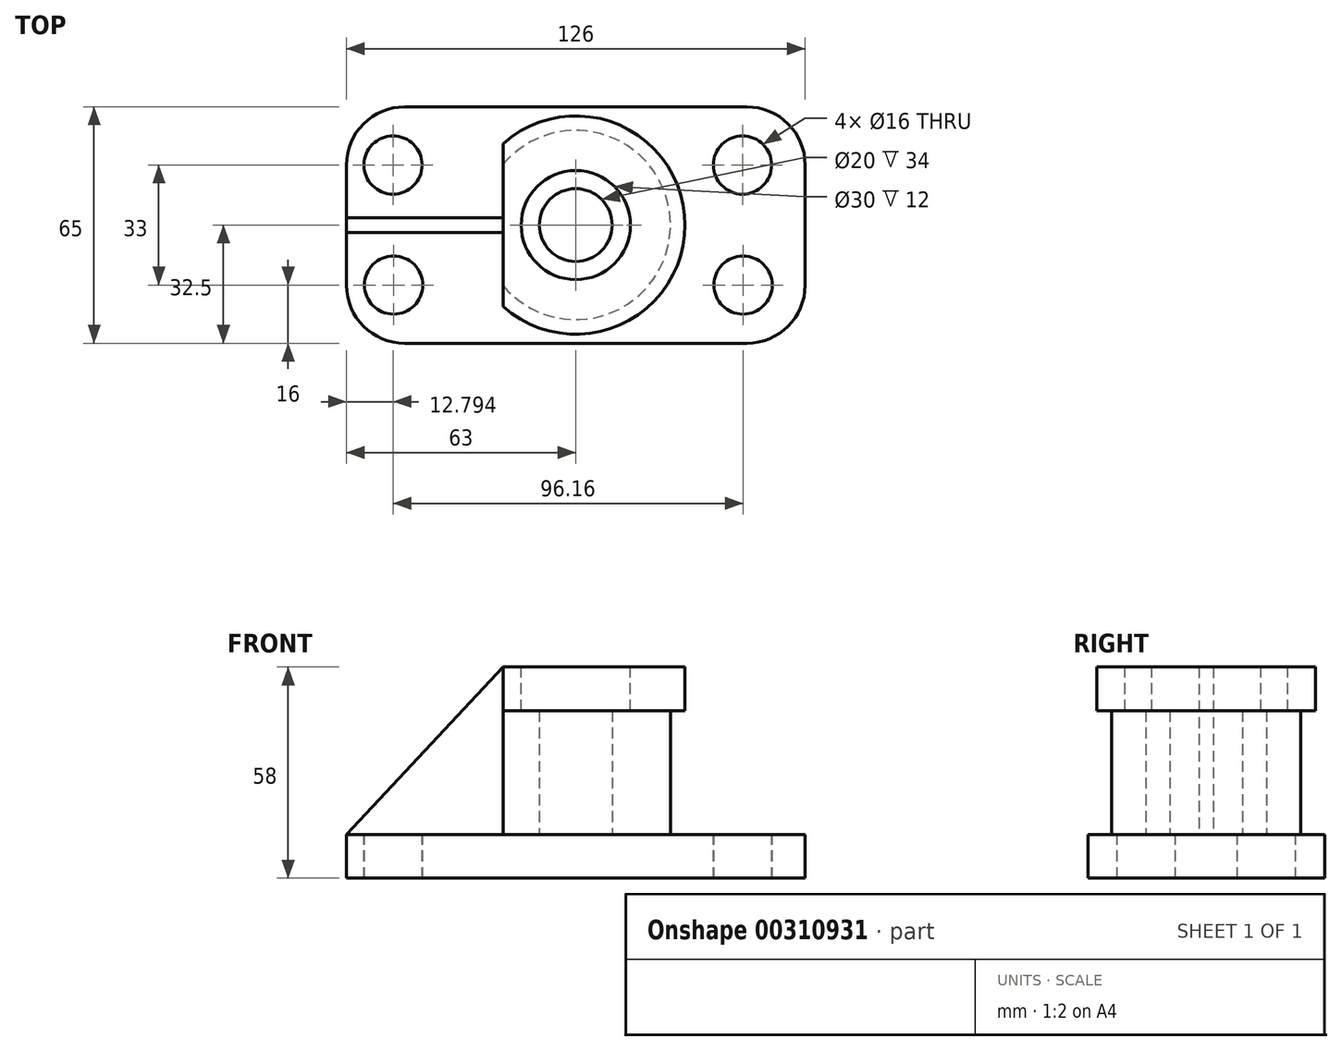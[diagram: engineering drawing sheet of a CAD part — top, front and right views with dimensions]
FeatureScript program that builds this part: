
annotation { "Feature Type Name" : "Feature", "Feature Type Description" : "" }
export const myFeature = defineFeature(function(context is Context, id is Id, definition is map)
    precondition{}
    {
        {
            var Q0;
            Q0=qCreatedBy(makeId("Top.planeOp"),FACE);
            var sketch = newSketch(context, id + "F0", { "sketchPlane" : qUnion([Q0])});
            skCircle(sketch, "E0", {"center": v(0, 0) * mm, "radius": 26 * mm});
            skCircle(sketch, "E1", {"center": v(0, 0) * mm, "radius": 10 * mm});
            skPoint(sketch, "E2", {"position": v(-10, 0) * mm});
            skLineSegment(sketch, "E3", {"start": v(-10, 24) * mm, "end": v(-10, -24) * mm});
            skSolve(sketch);
        }
        {
            var Q0;
            Q0 = qSketchRegion(id + "F0", true);
            extrude(context, id + "F1", {"entities" : qUnion([Q0]), "depth" : 58 * mm});
        }
        {
            var Q0;
            Q0=makeQuery(id+"F1.opExtrude","CAP_FACE",FACE,{"disambiguationData":[OSD([sQuery(id+"F0.wireOp",EDGE,"E0"),sQuery(id+"F0.wireOp",EDGE,"E1")])],"isStart":true});
            var sketch = newSketch(context, id + "F2", { "sketchPlane" : qUnion([Q0])});
            skLineSegment(sketch, "E4", {"start": v(0, 32.5) * mm, "end": v(-63, 32.5) * mm});
            skLineSegment(sketch, "E5", {"start": v(-63, 32.5) * mm, "end": v(-63, -32.5) * mm});
            skLineSegment(sketch, "E6", {"start": v(-63, -32.5) * mm, "end": v(63, -32.5) * mm});
            skLineSegment(sketch, "E7", {"start": v(63, 32.5) * mm, "end": v(63, -32.5) * mm});
            skLineSegment(sketch, "E8", {"start": v(63, 32.5) * mm, "end": v(0, 32.5) * mm});
            skPoint(sketch, "E9.end.orphan", {"position": v(-63, 0) * mm});
            skPoint(sketch, "E10.end.orphan", {"position": v(0, 0) * mm});
            skSolve(sketch);
        }
        {
            var Q0;
            Q0 = qSketchRegion(id + "F2", true);
            extrude(context, id + "F3", {"entities" : qUnion([Q0]), "operationType" : NewBodyOperationType.ADD, "oppositeDirection" : true, "depth" : 12 * mm});
        }
        {
            var Q0;
            {var subQ0=sQuery(id+"F2.wireOp",EDGE,"E6");var subQ1=sQuery(id+"F2.wireOp",EDGE,"E5");var subQ2=sQuery(id+"F2.wireOp",EDGE,"E8");var subQ3=sQuery(id+"F2.wireOp",EDGE,"E4");var subQ4=sQuery(id+"F2.wireOp",EDGE,"E7");Q0=makeQuery(id+"F3.boolean.opBoolean","SPLIT",FACE,{"disambiguationData":[TD([makeQuery(id+"F1.opExtrude","SWEPT_FACE",FACE,{"disambiguationData":[OSD([sQuery(id+"F0.wireOp",EDGE,"E0")])]})])],"derivedFrom":makeQuery(id+"F3.opExtrude","CAP_FACE",FACE,{"disambiguationData":[OSD([subQ3,subQ1,subQ0,subQ4,subQ2])],"isStart":false})});}
            var sketch = newSketch(context, id + "F4", { "sketchPlane" : qUnion([Q0])});
            skCircle(sketch, "E11", {"center": v(-50.05, -16.5) * mm, "radius": 8 * mm});
            skCircle(sketch, "E12", {"center": v(-50.2, 16.5) * mm, "radius": 8 * mm});
            skCircle(sketch, "E13", {"center": v(45.8, 16.5) * mm, "radius": 8 * mm});
            skCircle(sketch, "E14", {"center": v(45.95, -16.5) * mm, "radius": 8 * mm});
            skPoint(sketch, "E15.end.orphan", {"position": v(-63, 0) * mm});
            skPoint(sketch, "E15.start.orphan", {"position": v(0, 0) * mm});
            skSolve(sketch);
        }
        {
            var Q0;
            Q0 = qSketchRegion(id + "F4", true);
            extrude(context, id + "F5", {"entities" : qUnion([Q0]), "operationType" : NewBodyOperationType.REMOVE, "oppositeDirection" : true, "depth" : 25 * mm});
        }
        {
            var Q0;
            Q0=makeQuery(id+"F3.opExtrude","SWEPT_EDGE",EDGE,{"disambiguationData":[OSD([sQuery(id+"F2.wireOp",EDGE,"E5"),sQuery(id+"F2.wireOp",EDGE,"E6")])]});
            var Q1;
            Q1=makeQuery(id+"F3.opExtrude","SWEPT_EDGE",EDGE,{"disambiguationData":[OSD([sQuery(id+"F2.wireOp",EDGE,"E4"),sQuery(id+"F2.wireOp",EDGE,"E5")])]});
            var Q2;
            Q2=makeQuery(id+"F3.opExtrude","SWEPT_EDGE",EDGE,{"disambiguationData":[OSD([sQuery(id+"F2.wireOp",EDGE,"E6"),sQuery(id+"F2.wireOp",EDGE,"E7")])]});
            var Q3;
            Q3=makeQuery(id+"F3.opExtrude","SWEPT_EDGE",EDGE,{"disambiguationData":[OSD([sQuery(id+"F2.wireOp",EDGE,"E7"),sQuery(id+"F2.wireOp",EDGE,"E8")])]});
            fillet(context, id + "F6", {"entities" : qUnion([Q0, Q1, Q2, Q3]), "radius" : 16 * mm, "tangentPropagation" : true, "allowEdgeOverflow" : false});
        }
        {
            var Q0;
            Q0=makeQuery(id+"F1.opExtrude","CAP_FACE",FACE,{"disambiguationData":[OSD([sQuery(id+"F0.wireOp",EDGE,"E0"),sQuery(id+"F0.wireOp",EDGE,"E1")])],"isStart":false});
            var sketch = newSketch(context, id + "F7", { "sketchPlane" : qUnion([Q0])});
            skCircle(sketch, "E16", {"center": v(0, 0) * mm, "radius": 30 * mm});
            skPoint(sketch, "E17", {"position": v(-26, 0) * mm});
            skLineSegment(sketch, "E18", {"start": v(-20, 22.36) * mm, "end": v(-20, -22.36) * mm});
            skSolve(sketch);
        }
        {
            var Q0;
            Q0=makeQuery(id+"F7.imprint","IMPRINT",FACE,{"disambiguationData":[TD([[makeQuery(id+"F7.imprint","IMPRINT",EDGE,{"derivedFrom":makeQuery(id+"F1.opExtrude","CAP_EDGE",EDGE,{"disambiguationData":[OSD([sQuery(id+"F0.wireOp",EDGE,"E1")])],"isStart":false})}),1.0]])]});
            var Q1;
            {var subQ4=makeQuery(id+"F1.opExtrude","CAP_EDGE",EDGE,{"disambiguationData":[OSD([sQuery(id+"F0.wireOp",EDGE,"E0")])],"isStart":false});Q1=makeQuery(id+"F7.imprint","IMPRINT",FACE,{"disambiguationData":[TD([[makeQuery(id+"F7.imprint","IMPRINT",EDGE,{"derivedFrom":subQ4}),-1.0]])]});}
            var Q2;
            Q2=makeQuery(id+"F7.imprint","IMPRINT",FACE,{"disambiguationData":[TD([[makeQuery(id+"F7.imprint","IMPRINT",EDGE,{"derivedFrom":makeQuery(id+"F1.opExtrude","CAP_EDGE",EDGE,{"disambiguationData":[OSD([sQuery(id+"F0.wireOp",EDGE,"E0")])],"isStart":false})}),1.0]])]});
            extrude(context, id + "F8", {"entities" : qUnion([Q0, Q1, Q2]), "operationType" : NewBodyOperationType.ADD, "oppositeDirection" : true, "depth" : 12 * mm});
        }
        {
            var Q0;
            Q0=makeQuery(id+"F7.imprint","IMPRINT",FACE,{"disambiguationData":[TD([[makeQuery(id+"F7.imprint","IMPRINT",EDGE,{"derivedFrom":makeQuery(id+"F1.opExtrude","CAP_EDGE",EDGE,{"disambiguationData":[OSD([sQuery(id+"F0.wireOp",EDGE,"E0")])],"isStart":false})}),1.0]])]});
            var sketch = newSketch(context, id + "F9", { "sketchPlane" : qUnion([Q0])});
            skCircle(sketch, "E19", {"center": v(0, 0) * mm, "radius": 15 * mm});
            skSolve(sketch);
        }
        {
            var Q0;
            Q0=makeQuery(id+"F9.imprint","IMPRINT",FACE,{"disambiguationData":[TD([[makeQuery(id+"F9.imprint","IMPRINT",EDGE,{"derivedFrom":makeQuery(id+"F7.imprint","IMPRINT",EDGE,{"derivedFrom":makeQuery(id+"F1.opExtrude","CAP_EDGE",EDGE,{"disambiguationData":[OSD([sQuery(id+"F0.wireOp",EDGE,"E1")])],"isStart":false})})}),1.0]])]});
            var Q1;
            Q1=makeQuery(id+"F9.imprint","IMPRINT",FACE,{"disambiguationData":[TD([[makeQuery(id+"F9.imprint","IMPRINT",EDGE,{"derivedFrom":sQuery(id+"F9.wireOp",EDGE,"E19")}),1.0]])]});
            extrude(context, id + "F10", {"entities" : qUnion([Q0, Q1]), "operationType" : NewBodyOperationType.REMOVE, "oppositeDirection" : true, "depth" : 12 * mm});
        }
        {
            var Q0;
            {var subQ0=sQuery(id+"F7.wireOp",EDGE,"E18");var subQ1=sQuery(id+"F7.wireOp",EDGE,"E16");var subQ2=makeQuery(id+"F7.imprint","INTERSECT",VERTEX,{"disambiguationData":[OD(0.0)],"derivedFrom":[subQ1,subQ0]});Q0=makeQuery(id+"F7.imprint","IMPRINT",FACE,{"disambiguationData":[TD([[makeQuery(id+"F7.imprint","IMPRINT",EDGE,{"disambiguationData":[TD([[subQ2,-1.0]])],"derivedFrom":subQ1}),1.0]])]});}
            var Q1;
            {var subQ0=sQuery(id+"F7.wireOp",EDGE,"E18");var subQ1=makeQuery(id+"F1.opExtrude","CAP_EDGE",EDGE,{"disambiguationData":[OSD([sQuery(id+"F0.wireOp",EDGE,"E0")])],"isStart":false});var subQ2=makeQuery(id+"F7.imprint","INTERSECT",VERTEX,{"disambiguationData":[OD(0.0)],"derivedFrom":[subQ1,subQ0]});Q1=makeQuery(id+"F7.imprint","IMPRINT",FACE,{"disambiguationData":[TD([[makeQuery(id+"F7.imprint","IMPRINT",EDGE,{"disambiguationData":[TD([[subQ2,-1.0]])],"derivedFrom":subQ0}),-1.0]])]});}
            extrude(context, id + "F11", {"entities" : qUnion([Q0, Q1]), "operationType" : NewBodyOperationType.REMOVE, "oppositeDirection" : true, "depth" : 46 * mm});
        }
        {
            var Q0;
            {var subQ0=sQuery(id+"F2.wireOp",EDGE,"E6");var subQ1=sQuery(id+"F2.wireOp",EDGE,"E5");var subQ2=sQuery(id+"F2.wireOp",EDGE,"E8");var subQ3=sQuery(id+"F2.wireOp",EDGE,"E4");var subQ4=sQuery(id+"F2.wireOp",EDGE,"E7");Q0=makeQuery(id+"F11.boolean.opBoolean","MERGE",FACE,{"derivedFrom":[makeQuery(id+"F3.boolean.opBoolean","SPLIT",FACE,{"disambiguationData":[TD([makeQuery(id+"F1.opExtrude","SWEPT_FACE",FACE,{"disambiguationData":[OSD([sQuery(id+"F0.wireOp",EDGE,"E0")])]})])],"derivedFrom":makeQuery(id+"F3.opExtrude","CAP_FACE",FACE,{"disambiguationData":[OSD([subQ3,subQ1,subQ0,subQ4,subQ2])],"isStart":false})}),makeQuery(id+"F11.opExtrude","CAP_FACE",FACE,{"disambiguationData":[OSD([sQuery(id+"F7.wireOp",EDGE,"E16"),sQuery(id+"F7.wireOp",EDGE,"E18")])],"isStart":false})]});}
            var sketch = newSketch(context, id + "F12", { "sketchPlane" : qUnion([Q0])});
            skLineSegment(sketch, "E20.0", {"start": v(0, 2) * mm, "end": v(-63, 2) * mm});
            skLineSegment(sketch, "E21.0", {"start": v(0, -2) * mm, "end": v(-63, -2) * mm});
            skLineSegment(sketch, "E22", {"start": v(0, 0) * mm, "end": v(-63, 0) * mm, "construction": true});
            skLineSegment(sketch, "E23", {"start": v(-63, 2) * mm, "end": v(-63, -2) * mm});
            skLineSegment(sketch, "E24.0", {"start": v(-20, 22.36) * mm, "end": v(-20, -22.36) * mm});
            skSolve(sketch);
        }
        {
            var Q0;
            Q0 = qSketchRegion(id + "F12", true);
            extrude(context, id + "F13", {"entities" : qUnion([Q0]), "operationType" : NewBodyOperationType.ADD, "depth" : 46 * mm});
        }
        {
            var Q0;
            Q0=makeQuery(id+"F13.opExtrude","SWEPT_FACE",FACE,{"disambiguationData":[OSD([sQuery(id+"F12.wireOp",EDGE,"E21.0")])]});
            var sketch = newSketch(context, id + "F14", { "sketchPlane" : qUnion([Q0])});
            skLineSegment(sketch, "E25", {"start": v(-20, 58) * mm, "end": v(-63, 12) * mm});
            skSolve(sketch);
        }
        {
            var Q0;
            Q0 = qSketchRegion(id + "F14", true);
            var Q1;
            Q1=makeQuery(id+"F14.imprint","IMPRINT",FACE,{"disambiguationData":[TD([[makeQuery(id+"F14.imprint","IMPRINT",EDGE,{"derivedFrom":sQuery(id+"F14.wireOp",EDGE,"E25")}),-1.0]])]});
            extrude(context, id + "F15", {"entities" : qUnion([Q0, Q1]), "operationType" : NewBodyOperationType.REMOVE, "oppositeDirection" : true, "depth" : 25 * mm});
        }
    });
